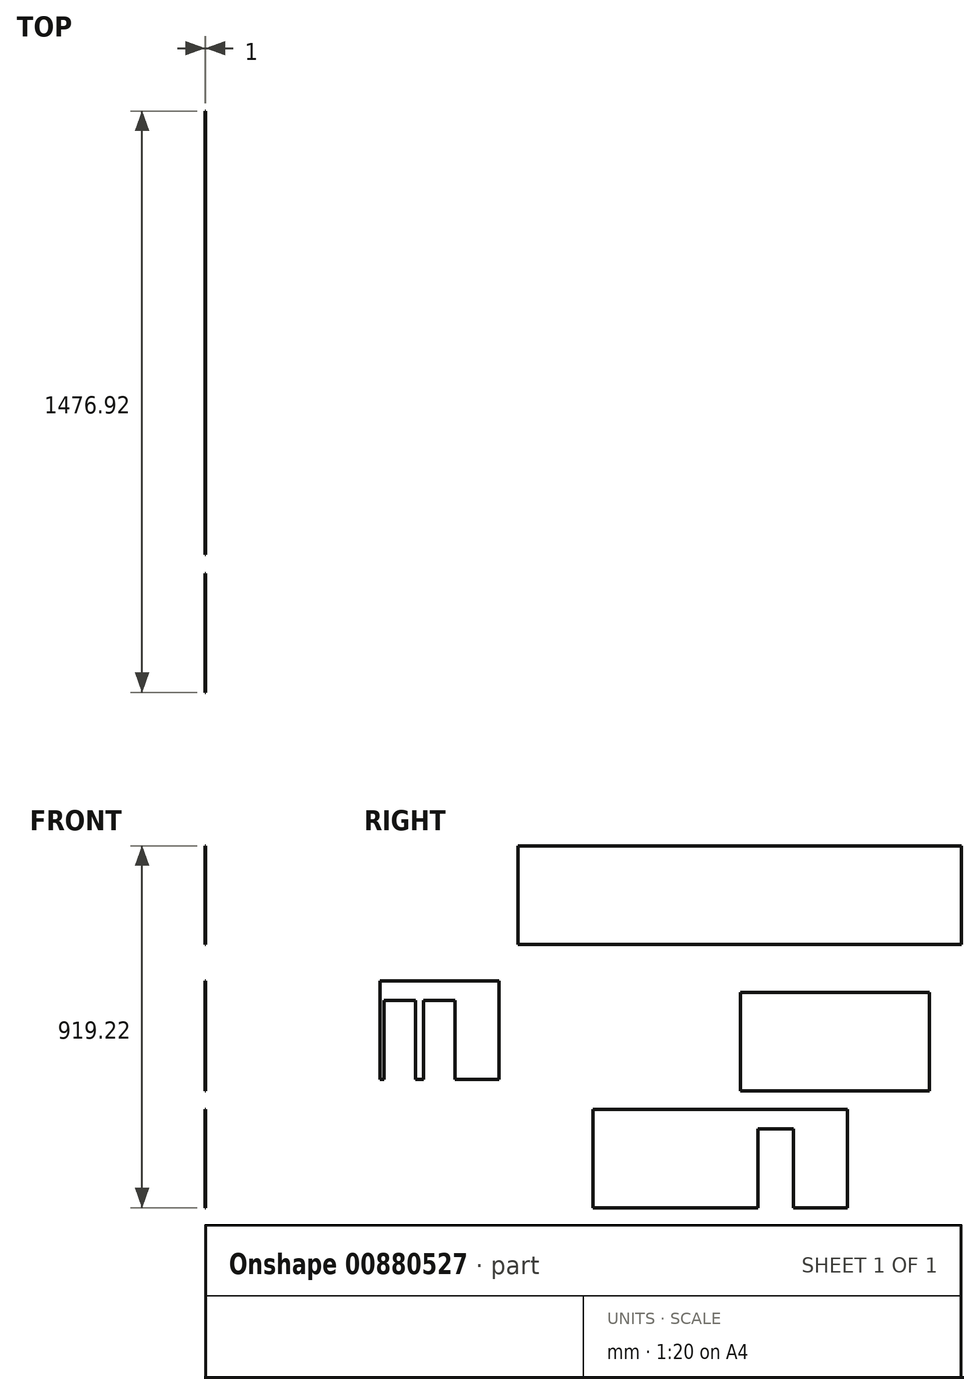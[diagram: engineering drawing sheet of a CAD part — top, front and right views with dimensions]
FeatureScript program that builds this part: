
annotation { "Feature Type Name" : "Feature", "Feature Type Description" : "" }
export const myFeature = defineFeature(function(context is Context, id is Id, definition is map)
    precondition{}
    {
        {
            var Q0;
            Q0=qCreatedBy(makeId("Right.planeOp"),FACE);
            var sketch = newSketch(context, id + "F0", { "sketchPlane" : qUnion([Q0])});
            skLineSegment(sketch, "E0.bottom", {"start": v(-939.85, 343.18) * mm, "end": v(187.15, 343.18) * mm});
            skLineSegment(sketch, "E0.top", {"start": v(-939.85, 93.18) * mm, "end": v(187.15, 93.18) * mm});
            skLineSegment(sketch, "E0.left", {"start": v(-939.85, 343.18) * mm, "end": v(-939.85, 93.18) * mm});
            skLineSegment(sketch, "E0.right", {"start": v(187.15, 343.18) * mm, "end": v(187.15, 93.18) * mm});
            skLineSegment(sketch, "E1.bottom", {"start": v(-1289.77, 0) * mm, "end": v(-987.77, 0) * mm});
            skLineSegment(sketch, "E1.top", {"start": v(-1289.77, -250) * mm, "end": v(-987.77, -250) * mm});
            skLineSegment(sketch, "E1.left", {"start": v(-1289.77, 0) * mm, "end": v(-1289.77, -250) * mm});
            skLineSegment(sketch, "E1.right", {"start": v(-987.77, 0) * mm, "end": v(-987.77, -250) * mm});
            skLineSegment(sketch, "E2.bottom", {"start": v(-374.66, -29.73) * mm, "end": v(105.34, -29.73) * mm});
            skLineSegment(sketch, "E2.top", {"start": v(-374.66, -279.73) * mm, "end": v(105.34, -279.73) * mm});
            skLineSegment(sketch, "E2.left", {"start": v(-374.66, -29.73) * mm, "end": v(-374.66, -279.73) * mm});
            skLineSegment(sketch, "E2.right", {"start": v(105.34, -29.73) * mm, "end": v(105.34, -279.73) * mm});
            skLineSegment(sketch, "E3.bottom", {"start": v(-749.48, -326.04) * mm, "end": v(-102.48, -326.04) * mm});
            skLineSegment(sketch, "E3.top", {"start": v(-749.48, -576.04) * mm, "end": v(-102.48, -576.04) * mm});
            skLineSegment(sketch, "E3.left", {"start": v(-749.48, -326.04) * mm, "end": v(-749.48, -576.04) * mm});
            skLineSegment(sketch, "E3.right", {"start": v(-102.48, -326.04) * mm, "end": v(-102.48, -576.04) * mm});
            skLineSegment(sketch, "E4", {"start": v(-329.48, -576.04) * mm, "end": v(-329.48, -376.04) * mm});
            skLineSegment(sketch, "E5", {"start": v(-329.48, -376.04) * mm, "end": v(-239.48, -376.04) * mm});
            skLineSegment(sketch, "E6", {"start": v(-239.48, -376.04) * mm, "end": v(-239.48, -576.04) * mm});
            skLineSegment(sketch, "E7", {"start": v(-1279.77, -250) * mm, "end": v(-1279.77, -50) * mm});
            skLineSegment(sketch, "E8", {"start": v(-1279.77, -50) * mm, "end": v(-1199.77, -50) * mm});
            skLineSegment(sketch, "E9", {"start": v(-1199.77, -50) * mm, "end": v(-1199.77, -250) * mm});
            skLineSegment(sketch, "E10", {"start": v(-1179.77, -250) * mm, "end": v(-1179.77, -50) * mm});
            skLineSegment(sketch, "E11", {"start": v(-1179.77, -50) * mm, "end": v(-1099.77, -50) * mm});
            skLineSegment(sketch, "E12", {"start": v(-1099.77, -50) * mm, "end": v(-1099.77, -250) * mm});
            skSolve(sketch);
        }
        {
            var Q0;
            Q0=makeQuery(id+"F0.imprint","IMPRINT",FACE,{"disambiguationData":[TD([[makeQuery(id+"F0.imprint","IMPRINT",EDGE,{"derivedFrom":sQuery(id+"F0.wireOp",EDGE,"E0.bottom")}),-1.0]])]});
            var Q1;
            Q1=makeQuery(id+"F0.imprint","IMPRINT",FACE,{"disambiguationData":[TD([[makeQuery(id+"F0.imprint","IMPRINT",EDGE,{"derivedFrom":sQuery(id+"F0.wireOp",EDGE,"E1.bottom")}),-1.0]])]});
            var Q2;
            Q2=makeQuery(id+"F0.imprint","IMPRINT",FACE,{"disambiguationData":[TD([[makeQuery(id+"F0.imprint","IMPRINT",EDGE,{"derivedFrom":sQuery(id+"F0.wireOp",EDGE,"E2.bottom")}),-1.0]])]});
            var Q3;
            Q3=makeQuery(id+"F0.imprint","IMPRINT",FACE,{"disambiguationData":[TD([[makeQuery(id+"F0.imprint","IMPRINT",EDGE,{"derivedFrom":sQuery(id+"F0.wireOp",EDGE,"E3.bottom")}),-1.0]])]});
            extrude(context, id + "F1", {"entities" : qUnion([Q0, Q1, Q2, Q3]), "depth" : 1 * mm, "offsetDistance" : 25 * mm});
        }
    });
